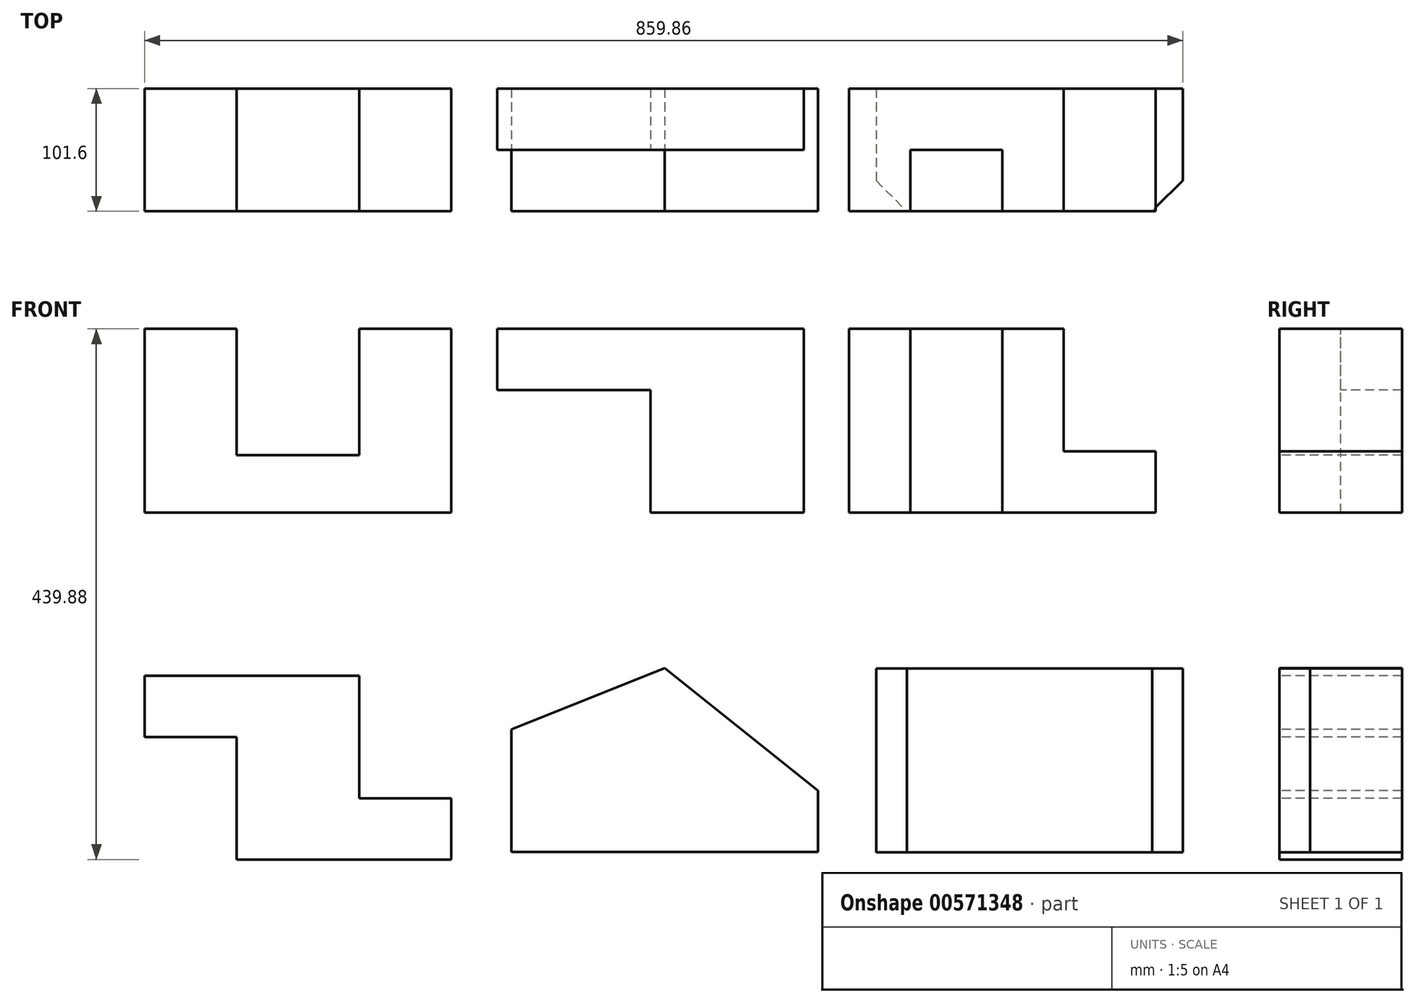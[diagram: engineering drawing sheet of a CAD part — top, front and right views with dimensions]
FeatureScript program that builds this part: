
annotation { "Feature Type Name" : "Feature", "Feature Type Description" : "" }
export const myFeature = defineFeature(function(context is Context, id is Id, definition is map)
    precondition{}
    {
        {
            var Q0;
            Q0=qCreatedBy(makeId("Front.planeOp"),FACE);
            var sketch = newSketch(context, id + "F0", { "sketchPlane" : qUnion([Q0])});
            skLineSegment(sketch, "E0", {"start": v(254, 0) * mm, "end": v(254, 152.4) * mm});
            skLineSegment(sketch, "E1", {"start": v(254, 152.4) * mm, "end": v(177.8, 152.4) * mm});
            skLineSegment(sketch, "E2", {"start": v(177.8, 152.4) * mm, "end": v(177.8, 47.61) * mm});
            skLineSegment(sketch, "E3", {"start": v(177.8, 47.61) * mm, "end": v(76.2, 47.61) * mm});
            skLineSegment(sketch, "E4", {"start": v(76.2, 47.61) * mm, "end": v(76.2, 152.4) * mm});
            skLineSegment(sketch, "E5", {"start": v(76.2, 152.4) * mm, "end": v(0, 152.4) * mm});
            skLineSegment(sketch, "E6", {"start": v(0, 152.4) * mm, "end": v(0, 0) * mm});
            skLineSegment(sketch, "E7", {"start": v(0, 0) * mm, "end": v(254, 0) * mm});
            skSolve(sketch);
        }
        {
            var Q0;
            Q0=makeQuery(id+"F0.imprint","IMPRINT",FACE,{"disambiguationData":[TD([[makeQuery(id+"F0.imprint","IMPRINT",EDGE,{"derivedFrom":sQuery(id+"F0.wireOp",EDGE,"E0")}),1.0]])]});
            extrude(context, id + "F1", {"entities" : qUnion([Q0]), "oppositeDirection" : true, "depth" : 101.6 * mm, "offsetDistance" : 25.4 * mm});
        }
        {
            var Q0;
            Q0=qCreatedBy(makeId("Front.planeOp"),FACE);
            var sketch = newSketch(context, id + "F2", { "sketchPlane" : qUnion([Q0])});
            skLineSegment(sketch, "E8", {"start": v(292.06, 0) * mm, "end": v(292.06, 152.4) * mm});
            skLineSegment(sketch, "E9", {"start": v(292.06, 152.4) * mm, "end": v(546.06, 152.4) * mm});
            skLineSegment(sketch, "E10", {"start": v(546.06, 152.4) * mm, "end": v(546.06, 0) * mm});
            skLineSegment(sketch, "E11", {"start": v(546.06, 0) * mm, "end": v(292.06, 0) * mm});
            skLineSegment(sketch, "E12", {"start": v(292.06, 0) * mm, "end": v(419.06, 0) * mm});
            skLineSegment(sketch, "E13", {"start": v(419.06, 0) * mm, "end": v(419.06, 101.6) * mm});
            skLineSegment(sketch, "E14", {"start": v(419.06, 101.6) * mm, "end": v(292.06, 101.6) * mm});
            skSolve(sketch);
        }
        {
            var Q0;
            {var subQ0=sQuery(id+"F2.wireOp",EDGE,"E9");Q0=makeQuery(id+"F2.imprint","IMPRINT",FACE,{"disambiguationData":[TD([[makeQuery(id+"F2.imprint","IMPRINT",EDGE,{"derivedFrom":subQ0}),-1.0]])]});}
            var Q1;
            {var subQ0=sQuery(id+"F2.wireOp",EDGE,"E12");Q1=makeQuery(id+"F2.imprint","IMPRINT",FACE,{"disambiguationData":[TD([[makeQuery(id+"F2.imprint","IMPRINT",EDGE,{"derivedFrom":subQ0}),1.0]])]});}
            extrude(context, id + "F3", {"entities" : qUnion([Q0, Q1]), "oppositeDirection" : true, "depth" : 101.6 * mm, "offsetDistance" : 25.4 * mm});
        }
        {
            var Q0;
            Q0=makeQuery(id+"F3.opExtrude","SWEPT_FACE",FACE,{"disambiguationData":[OSD([sQuery(id+"F2.wireOp",EDGE,"E9")])]});
            var sketch = newSketch(context, id + "F4", { "sketchPlane" : qUnion([Q0])});
            skPoint(sketch, "E15.oppositeSnap0", {"position": v(292.06, 50.8) * mm});
            skLineSegment(sketch, "E15.bottom", {"start": v(546.06, 0) * mm, "end": v(419.06, 0) * mm});
            skLineSegment(sketch, "E15.top", {"start": v(546.06, 50.8) * mm, "end": v(419.06, 50.8) * mm});
            skLineSegment(sketch, "E15.left", {"start": v(546.06, 0) * mm, "end": v(546.06, 50.8) * mm});
            skLineSegment(sketch, "E15.right", {"start": v(419.06, 0) * mm, "end": v(419.06, 50.8) * mm});
            skSolve(sketch);
        }
        {
            var Q0;
            Q0=makeQuery(id+"F4.imprint","IMPRINT",FACE,{"disambiguationData":[TD([[makeQuery(id+"F4.imprint","IMPRINT",EDGE,{"derivedFrom":sQuery(id+"F4.wireOp",EDGE,"E15.bottom")}),1.0]])]});
            extrude(context, id + "F5", {"entities" : qUnion([Q0]), "operationType" : NewBodyOperationType.REMOVE, "oppositeDirection" : true, "depth" : 152.4 * mm, "offsetDistance" : 25.4 * mm});
        }
        {
            var Q0;
            Q0=makeQuery(id+"F3.opExtrude","CAP_FACE",FACE,{"disambiguationData":[OSD([sQuery(id+"F2.wireOp",EDGE,"E8"),sQuery(id+"F2.wireOp",EDGE,"E9"),sQuery(id+"F2.wireOp",EDGE,"E10"),sQuery(id+"F2.wireOp",EDGE,"E11"),sQuery(id+"F2.wireOp",EDGE,"E12")])],"isStart":true});
            var sketch = newSketch(context, id + "F6", { "sketchPlane" : qUnion([Q0])});
            skLineSegment(sketch, "E16.bottom", {"start": v(292.06, 152.4) * mm, "end": v(419.06, 152.4) * mm});
            skLineSegment(sketch, "E16.top", {"start": v(292.06, 101.6) * mm, "end": v(419.06, 101.6) * mm});
            skLineSegment(sketch, "E16.left", {"start": v(292.06, 152.4) * mm, "end": v(292.06, 101.6) * mm});
            skLineSegment(sketch, "E16.right", {"start": v(419.06, 152.4) * mm, "end": v(419.06, 101.6) * mm});
            skSolve(sketch);
        }
        {
            var Q0;
            Q0=makeQuery(id+"F6.imprint","IMPRINT",FACE,{"disambiguationData":[TD([[makeQuery(id+"F6.imprint","IMPRINT",EDGE,{"derivedFrom":sQuery(id+"F6.wireOp",EDGE,"E16.bottom")}),-1.0]])]});
            extrude(context, id + "F7", {"entities" : qUnion([Q0]), "operationType" : NewBodyOperationType.REMOVE, "oppositeDirection" : true, "depth" : 50.8 * mm, "offsetDistance" : 25.4 * mm});
        }
        {
            var Q0;
            Q0=qCreatedBy(makeId("Front.planeOp"),FACE);
            var sketch = newSketch(context, id + "F8", { "sketchPlane" : qUnion([Q0])});
            skLineSegment(sketch, "E17", {"start": v(545.42, 0) * mm, "end": v(583.52, 0) * mm});
            skLineSegment(sketch, "E18", {"start": v(583.52, 0) * mm, "end": v(583.52, 152.4) * mm});
            skLineSegment(sketch, "E19", {"start": v(583.52, 152.4) * mm, "end": v(761.32, 152.4) * mm});
            skLineSegment(sketch, "E20", {"start": v(761.32, 152.4) * mm, "end": v(761.32, 50.8) * mm});
            skLineSegment(sketch, "E21", {"start": v(761.32, 50.8) * mm, "end": v(837.52, 50.8) * mm});
            skLineSegment(sketch, "E22", {"start": v(837.52, 50.8) * mm, "end": v(837.52, 0) * mm});
            skLineSegment(sketch, "E23", {"start": v(837.52, 0) * mm, "end": v(583.52, 0) * mm});
            skSolve(sketch);
        }
        {
            var Q0;
            Q0=makeQuery(id+"F8.imprint","IMPRINT",FACE,{"disambiguationData":[TD([[makeQuery(id+"F8.imprint","IMPRINT",EDGE,{"derivedFrom":sQuery(id+"F8.wireOp",EDGE,"E18")}),-1.0]])]});
            extrude(context, id + "F9", {"entities" : qUnion([Q0]), "oppositeDirection" : true, "depth" : 101.6 * mm, "offsetDistance" : 25.4 * mm});
        }
        {
            var Q0;
            Q0=makeQuery(id+"F9.opExtrude","SWEPT_FACE",FACE,{"disambiguationData":[OSD([sQuery(id+"F8.wireOp",EDGE,"E19")])]});
            var sketch = newSketch(context, id + "F10", { "sketchPlane" : qUnion([Q0])});
            skLineSegment(sketch, "E24", {"start": v(583.52, 0) * mm, "end": v(634.32, 0) * mm});
            skLineSegment(sketch, "E25", {"start": v(634.32, 0) * mm, "end": v(634.32, 50.8) * mm});
            skLineSegment(sketch, "E26", {"start": v(634.32, 50.8) * mm, "end": v(710.52, 50.8) * mm});
            skLineSegment(sketch, "E27", {"start": v(710.52, 50.8) * mm, "end": v(710.52, 0) * mm});
            skSolve(sketch);
        }
        {
            var Q0;
            {var subQ0=sQuery(id+"F10.wireOp",EDGE,"E25");Q0=makeQuery(id+"F10.imprint","IMPRINT",FACE,{"disambiguationData":[TD([[makeQuery(id+"F10.imprint","IMPRINT",EDGE,{"derivedFrom":subQ0}),-1.0]])]});}
            extrude(context, id + "F11", {"entities" : qUnion([Q0]), "operationType" : NewBodyOperationType.REMOVE, "oppositeDirection" : true, "depth" : 152.4 * mm, "offsetDistance" : 25.4 * mm});
        }
        {
            var Q0;
            Q0=qCreatedBy(makeId("Front.planeOp"),FACE);
            var sketch = newSketch(context, id + "F12", { "sketchPlane" : qUnion([Q0])});
            skLineSegment(sketch, "E28", {"start": v(0, -135.08) * mm, "end": v(0, -185.88) * mm});
            skLineSegment(sketch, "E29", {"start": v(0, -135.08) * mm, "end": v(177.8, -135.08) * mm});
            skLineSegment(sketch, "E30", {"start": v(177.8, -135.08) * mm, "end": v(177.8, -236.68) * mm});
            skLineSegment(sketch, "E31", {"start": v(177.8, -236.68) * mm, "end": v(254, -236.68) * mm});
            skLineSegment(sketch, "E32", {"start": v(254, -236.68) * mm, "end": v(254, -287.48) * mm});
            skLineSegment(sketch, "E33", {"start": v(254, -287.48) * mm, "end": v(76.2, -287.48) * mm});
            skLineSegment(sketch, "E34", {"start": v(76.2, -287.48) * mm, "end": v(76.2, -185.88) * mm});
            skLineSegment(sketch, "E35", {"start": v(76.2, -185.88) * mm, "end": v(0, -185.88) * mm});
            skSolve(sketch);
        }
        {
            var Q0;
            Q0=makeQuery(id+"F12.imprint","IMPRINT",FACE,{"disambiguationData":[TD([[makeQuery(id+"F12.imprint","IMPRINT",EDGE,{"derivedFrom":sQuery(id+"F12.wireOp",EDGE,"E28")}),1.0]])]});
            extrude(context, id + "F13", {"entities" : qUnion([Q0]), "oppositeDirection" : true, "depth" : 101.6 * mm, "offsetDistance" : 25.4 * mm});
        }
        {
            var Q0;
            Q0=qCreatedBy(makeId("Front.planeOp"),FACE);
            var sketch = newSketch(context, id + "F14", { "sketchPlane" : qUnion([Q0])});
            skLineSegment(sketch, "E36", {"start": v(557.7, -281.21) * mm, "end": v(557.7, -230.41) * mm});
            skLineSegment(sketch, "E37", {"start": v(303.7, -281.21) * mm, "end": v(303.7, -179.61) * mm});
            skLineSegment(sketch, "E38", {"start": v(303.7, -179.61) * mm, "end": v(430.7, -128.81) * mm});
            skLineSegment(sketch, "E39", {"start": v(557.7, -230.41) * mm, "end": v(430.7, -128.81) * mm});
            skLineSegment(sketch, "E40", {"start": v(303.7, -281.21) * mm, "end": v(557.7, -281.21) * mm});
            skSolve(sketch);
        }
        {
            var Q0;
            Q0=makeQuery(id+"F14.imprint","IMPRINT",FACE,{"disambiguationData":[TD([[makeQuery(id+"F14.imprint","IMPRINT",EDGE,{"derivedFrom":sQuery(id+"F14.wireOp",EDGE,"E36")}),1.0]])]});
            extrude(context, id + "F15", {"entities" : qUnion([Q0]), "oppositeDirection" : true, "depth" : 101.6 * mm, "offsetDistance" : 25.4 * mm});
        }
        {
            var Q0;
            Q0=qCreatedBy(makeId("Front.planeOp"),FACE);
            var sketch = newSketch(context, id + "F16", { "sketchPlane" : qUnion([Q0])});
            skLineSegment(sketch, "E41", {"start": v(605.86, -281.62) * mm, "end": v(605.86, -129.22) * mm});
            skLineSegment(sketch, "E42", {"start": v(605.86, -129.22) * mm, "end": v(859.86, -129.22) * mm});
            skLineSegment(sketch, "E43", {"start": v(859.86, -129.22) * mm, "end": v(859.86, -281.62) * mm});
            skLineSegment(sketch, "E44", {"start": v(859.86, -281.62) * mm, "end": v(605.86, -281.62) * mm});
            skSolve(sketch);
        }
        {
            var Q0;
            Q0=makeQuery(id+"F16.imprint","IMPRINT",FACE,{"disambiguationData":[TD([[makeQuery(id+"F16.imprint","IMPRINT",EDGE,{"derivedFrom":sQuery(id+"F16.wireOp",EDGE,"E41")}),-1.0]])]});
            extrude(context, id + "F17", {"entities" : qUnion([Q0]), "oppositeDirection" : true, "depth" : 101.6 * mm, "offsetDistance" : 25.4 * mm});
        }
        {
            var Q0;
            Q0=makeQuery(id+"F17.opExtrude","SWEPT_FACE",FACE,{"disambiguationData":[OSD([sQuery(id+"F16.wireOp",EDGE,"E42")])]});
            var sketch = newSketch(context, id + "F18", { "sketchPlane" : qUnion([Q0])});
            skLineSegment(sketch, "E45", {"start": v(605.86, 0) * mm, "end": v(605.86, 25.4) * mm});
            skLineSegment(sketch, "E46", {"start": v(605.86, 0) * mm, "end": v(631.26, 0) * mm});
            skLineSegment(sketch, "E47", {"start": v(605.86, 25.4) * mm, "end": v(631.26, 0) * mm});
            skSolve(sketch);
        }
        {
            var Q0;
            Q0 = qSketchRegion(id + "F18", true);
            extrude(context, id + "F19", {"entities" : qUnion([Q0]), "operationType" : NewBodyOperationType.REMOVE, "oppositeDirection" : true, "depth" : 152.4 * mm, "offsetDistance" : 25.4 * mm});
        }
        {
            var Q0;
            Q0=makeQuery(id+"F17.opExtrude","SWEPT_FACE",FACE,{"disambiguationData":[OSD([sQuery(id+"F16.wireOp",EDGE,"E42")])]});
            var sketch = newSketch(context, id + "F20", { "sketchPlane" : qUnion([Q0])});
            skLineSegment(sketch, "E48", {"start": v(859.86, 0) * mm, "end": v(859.86, 25.4) * mm});
            skLineSegment(sketch, "E49", {"start": v(859.86, 0) * mm, "end": v(834.46, 0) * mm});
            skLineSegment(sketch, "E50", {"start": v(834.46, 0) * mm, "end": v(859.86, 25.4) * mm});
            skSolve(sketch);
        }
        {
            var Q0;
            Q0 = qSketchRegion(id + "F20", true);
            extrude(context, id + "F21", {"entities" : qUnion([Q0]), "operationType" : NewBodyOperationType.REMOVE, "oppositeDirection" : true, "depth" : 152.4 * mm, "offsetDistance" : 25.4 * mm});
        }
    });
